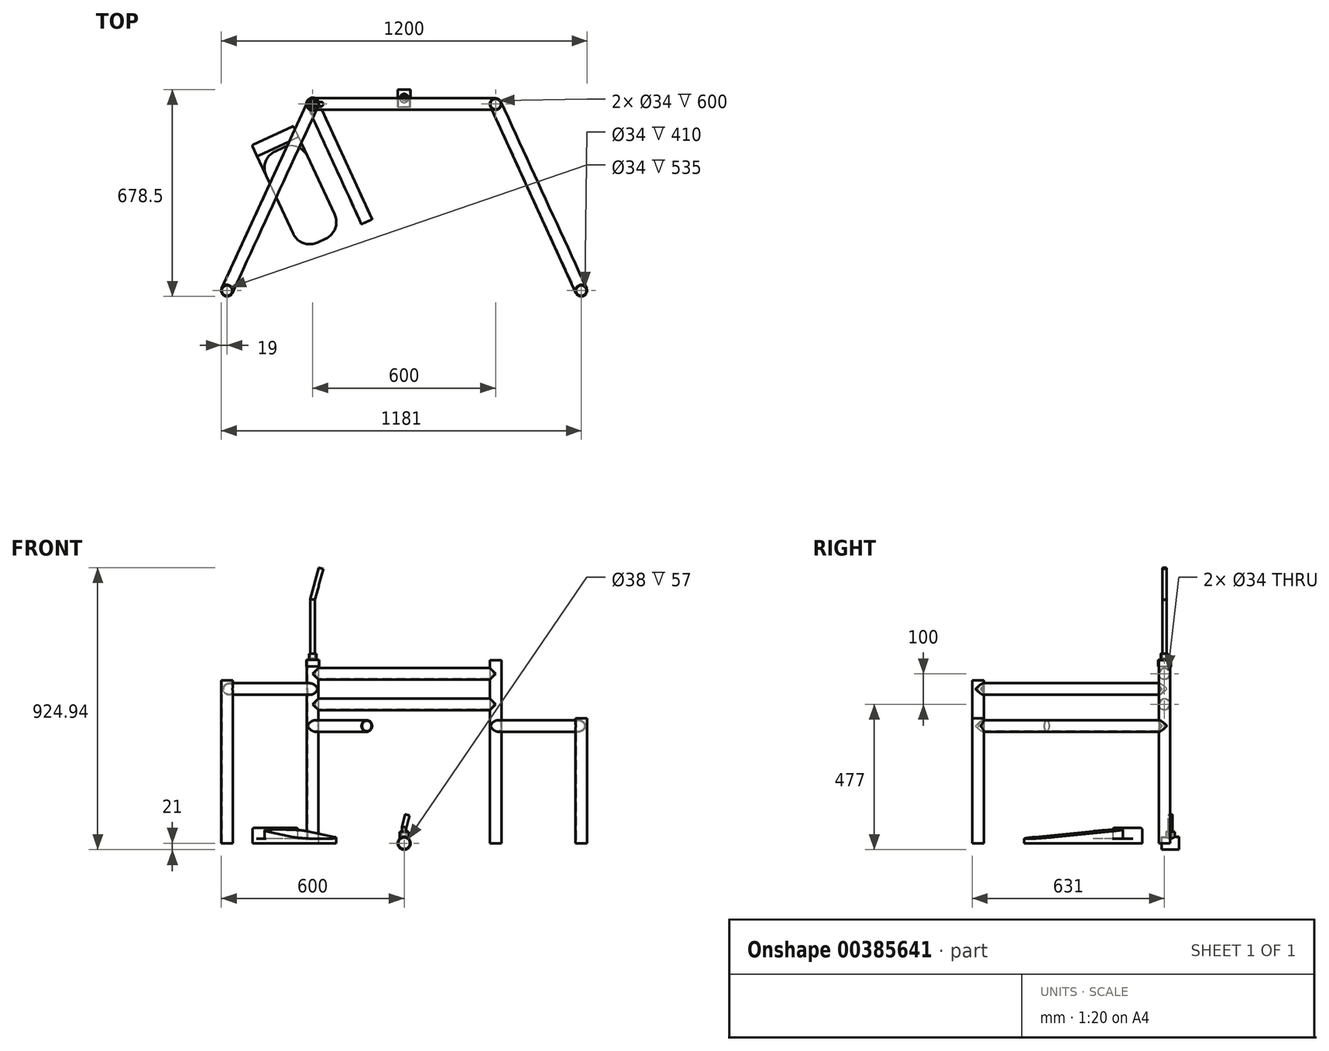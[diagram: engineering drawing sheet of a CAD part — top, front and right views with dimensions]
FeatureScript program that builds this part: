
annotation { "Feature Type Name" : "Feature", "Feature Type Description" : "" }
export const myFeature = defineFeature(function(context is Context, id is Id, definition is map)
    precondition{}
    {
        {
            assignVariable(context, id + "F0", {"name" : "tubo", "anyValue" : 38 * mm});
        }
        {
            var Q0;
            Q0=qCreatedBy(makeId("Top.planeOp"),FACE);
            var sketch = newSketch(context, id + "F1", { "sketchPlane" : qUnion([Q0])});
            skLineSegment(sketch, "E0.bottom", {"start": v(-600, 0) * mm, "end": v(600, 0) * mm});
            skLineSegment(sketch, "E0.top", {"start": v(-600, -650) * mm, "end": v(600, -650) * mm});
            skLineSegment(sketch, "E0.left", {"start": v(-600, 0) * mm, "end": v(-600, -650) * mm});
            skLineSegment(sketch, "E0.right", {"start": v(600, 0) * mm, "end": v(600, -650) * mm});
            skLineSegment(sketch, "E1.bottom", {"start": v(-650, 0) * mm, "end": v(650, 0) * mm});
            skLineSegment(sketch, "E1.top", {"start": v(-650, -1200) * mm, "end": v(650, -1200) * mm});
            skLineSegment(sketch, "E1.left", {"start": v(-650, 0) * mm, "end": v(-650, -1200) * mm});
            skLineSegment(sketch, "E1.right", {"start": v(650, 0) * mm, "end": v(650, -1200) * mm});
            skCircle(sketch, "E2", {"center": v(0, -1047.5) * mm, "radius": 152.5 * mm});
            skLineSegment(sketch, "E3.bottom", {"start": v(-581, -19) * mm, "end": v(581, -19) * mm, "construction": true});
            skLineSegment(sketch, "E3.top", {"start": v(-581, -631) * mm, "end": v(581, -631) * mm, "construction": true});
            skLineSegment(sketch, "E3.left", {"start": v(-581, -19) * mm, "end": v(-581, -631) * mm, "construction": true});
            skLineSegment(sketch, "E3.right", {"start": v(581, -19) * mm, "end": v(581, -631) * mm, "construction": true});
            skLineSegment(sketch, "E4.bottom", {"start": v(-300, -19) * mm, "end": v(300, -19) * mm, "construction": true});
            skLineSegment(sketch, "E4.top", {"start": v(-300, -631) * mm, "end": v(300, -631) * mm, "construction": true});
            skLineSegment(sketch, "E4.left", {"start": v(-300, -19) * mm, "end": v(-300, -631) * mm, "construction": true});
            skLineSegment(sketch, "E4.right", {"start": v(300, -19) * mm, "end": v(300, -631) * mm, "construction": true});
            skCircle(sketch, "E5", {"center": v(-581, -631) * mm, "radius": 19 * mm});
            skCircle(sketch, "E6", {"center": v(-581, -631) * mm, "radius": 17 * mm});
            skCircle(sketch, "E7", {"center": v(581, -631) * mm, "radius": 19 * mm});
            skCircle(sketch, "E8", {"center": v(581, -631) * mm, "radius": 17 * mm});
            skCircle(sketch, "E9", {"center": v(300, -19) * mm, "radius": 19 * mm});
            skCircle(sketch, "E10", {"center": v(300, -19) * mm, "radius": 17 * mm});
            skCircle(sketch, "E11", {"center": v(-300, -19) * mm, "radius": 19 * mm});
            skCircle(sketch, "E12", {"center": v(-300, -19) * mm, "radius": 17 * mm});
            skLineSegment(sketch, "E13", {"start": v(-300, -19) * mm, "end": v(-581, -631) * mm, "construction": true});
            skLineSegment(sketch, "E14", {"start": v(581, -631) * mm, "end": v(300, -19) * mm, "construction": true});
            skLineSegment(sketch, "E15", {"start": v(-476.85, -308.3) * mm, "end": v(-404.15, -341.7) * mm, "construction": true});
            skLineSegment(sketch, "E16", {"start": v(404.15, -341.7) * mm, "end": v(476.85, -308.3) * mm, "construction": true});
            skLineSegment(sketch, "E17", {"start": v(-300, -19) * mm, "end": v(-91.37, -473.4) * mm, "construction": true});
            skLineSegment(sketch, "E18", {"start": v(-136.8, -494.26) * mm, "end": v(-45.93, -452.53) * mm, "construction": true});
            skLineSegment(sketch, "E19", {"start": v(0, -1047.5) * mm, "end": v(-389.1, -213.06) * mm, "construction": true});
            skSolve(sketch);
        }
        {
            var Q0;
            Q0=makeQuery(id+"F1.imprint","IMPRINT",FACE,{"disambiguationData":[TD([[makeQuery(id+"F1.imprint","IMPRINT",EDGE,{"derivedFrom":sQuery(id+"F1.wireOp",EDGE,"E11")}),1.0]])]});
            var Q1;
            Q1=makeQuery(id+"F1.imprint","IMPRINT",FACE,{"disambiguationData":[TD([[makeQuery(id+"F1.imprint","IMPRINT",EDGE,{"derivedFrom":sQuery(id+"F1.wireOp",EDGE,"E9")}),1.0]])]});
            extrude(context, id + "F2", {"entities" : qUnion([Q0, Q1]), "depth" : 600 * mm});
        }
        {
            var Q0;
            Q0=makeQuery(id+"F1.imprint","IMPRINT",FACE,{"disambiguationData":[TD([[makeQuery(id+"F1.imprint","IMPRINT",EDGE,{"derivedFrom":sQuery(id+"F1.wireOp",EDGE,"E6")}),-1.0]])]});
            var Q1;
            Q1=makeQuery(id+"F1.imprint","IMPRINT",FACE,{"disambiguationData":[TD([[makeQuery(id+"F1.imprint","IMPRINT",EDGE,{"derivedFrom":sQuery(id+"F1.wireOp",EDGE,"E8")}),-1.0]])]});
            extrude(context, id + "F3", {"entities" : qUnion([Q0, Q1]), "depth" : 535 * mm});
        }
        {
            var Q0;
            Q0=qCreatedBy(makeId("Right.planeOp"),FACE);
            var sketch = newSketch(context, id + "F4", { "sketchPlane" : qUnion([Q0])});
            skCircle(sketch, "E20", {"center": v(-19, 556) * mm, "radius": 19 * mm});
            skCircle(sketch, "E21", {"center": v(-19, 556) * mm, "radius": 17 * mm});
            skLineSegment(sketch, "E22", {"start": v(-19, 556) * mm, "end": v(-19, 456) * mm, "construction": true});
            skCircle(sketch, "E23", {"center": v(-19, 456) * mm, "radius": 17 * mm});
            skCircle(sketch, "E24", {"center": v(-19, 456) * mm, "radius": 19 * mm});
            skLineSegment(sketch, "E25", {"start": v(-19, 556) * mm, "end": v(-19, 575) * mm, "construction": true});
            skPoint(sketch, "E26", {"position": v(-19, 506) * mm});
            skSolve(sketch);
        }
        {
            var Q0;
            Q0=makeQuery(id+"F4.imprint","IMPRINT",FACE,{"disambiguationData":[TD([[makeQuery(id+"F4.imprint","IMPRINT",EDGE,{"derivedFrom":sQuery(id+"F4.wireOp",EDGE,"E23")}),-1.0]])]});
            var Q1;
            Q1=makeQuery(id+"F4.imprint","IMPRINT",FACE,{"disambiguationData":[TD([[makeQuery(id+"F4.imprint","IMPRINT",EDGE,{"derivedFrom":sQuery(id+"F4.wireOp",EDGE,"E20")}),1.0]])]});
            var Q2;
            Q2=makeQuery(id+"F2.opExtrude","SWEPT_FACE",FACE,{"disambiguationData":[OSD([sQuery(id+"F1.wireOp",EDGE,"E9")])]});
            var Q3;
            Q3=makeQuery(id+"F2.opExtrude","SWEPT_FACE",FACE,{"disambiguationData":[OSD([sQuery(id+"F1.wireOp",EDGE,"E11")])]});
            extrude(context, id + "F5", {"entities" : qUnion([Q0, Q1]), "operationType" : NewBodyOperationType.ADD, "endBound" : BoundingType.UP_TO_SURFACE, "endBoundEntityFace" : qUnion([Q2]), "depth" : 25 * mm, "hasSecondDirection" : true, "secondDirectionBound" : SecondDirectionBoundingType.UP_TO_SURFACE, "secondDirectionOppositeDirection" : true, "secondDirectionBoundEntityFace" : qUnion([Q3]), "secondDirectionDepth" : 25 * mm});
        }
        {
            var Q0;
            Q0=sQuery(id+"F1.wireOp",EDGE,"E15");
            cPlane(context, id + "F6", {"entities" : qUnion([Q0]), "cplaneType" : CPlaneType.LINE_ANGLE, "offset" : 25 * mm, "angle" : 0 * degree, "width" : 150 * mm, "height" : 150 * mm});
        }
        {
            var Q0;
            Q0=qCreatedBy(id+"F6.planeOp",FACE);
            var sketch = newSketch(context, id + "F7", { "sketchPlane" : qUnion([Q0])});
            skCircle(sketch, "E27", {"center": v(264.7, 506) * mm, "radius": 19 * mm});
            skCircle(sketch, "E28", {"center": v(264.7, 506) * mm, "radius": 17 * mm});
            skLineSegment(sketch, "E29", {"start": v(264.7, 506) * mm, "end": v(264.7, 0) * mm, "construction": true});
            skLineSegment(sketch, "E30", {"start": v(264.7, 506) * mm, "end": v(264.7, 525) * mm, "construction": true});
            skSolve(sketch);
        }
        {
            var Q0;
            Q0=makeQuery(id+"F7.imprint","IMPRINT",FACE,{"disambiguationData":[TD([[makeQuery(id+"F7.imprint","IMPRINT",EDGE,{"derivedFrom":sQuery(id+"F7.wireOp",EDGE,"E27")}),1.0]])]});
            var Q1;
            {var subQ1=sQuery(id+"F1.wireOp",EDGE,"E11");Q1=makeQuery(id+"F5.boolean.opBoolean","SPLIT",FACE,{"disambiguationData":[TD([makeQuery(id+"F5.opExtrude","SWEPT_FACE",FACE,{"disambiguationData":[OSD([sQuery(id+"F4.wireOp",EDGE,"E20")])]})])],"derivedFrom":makeQuery(id+"F2.opExtrude","SWEPT_FACE",FACE,{"disambiguationData":[OSD([subQ1])]})});}
            var Q2;
            Q2=makeQuery(id+"F3.opExtrude","SWEPT_FACE",FACE,{"disambiguationData":[OSD([sQuery(id+"F1.wireOp",EDGE,"E5")])]});
            extrude(context, id + "F8", {"entities" : qUnion([Q0]), "operationType" : NewBodyOperationType.ADD, "endBound" : BoundingType.UP_TO_SURFACE, "endBoundEntityFace" : qUnion([Q1]), "depth" : 25 * mm, "hasSecondDirection" : true, "secondDirectionBound" : SecondDirectionBoundingType.UP_TO_SURFACE, "secondDirectionOppositeDirection" : true, "secondDirectionBoundEntityFace" : qUnion([Q2]), "secondDirectionDepth" : 25 * mm});
        }
        {
            var Q0;
            Q0=sQuery(id+"F1.wireOp",EDGE,"E16");
            cPlane(context, id + "F9", {"entities" : qUnion([Q0]), "cplaneType" : CPlaneType.LINE_ANGLE, "offset" : 25 * mm, "angle" : 0 * degree, "width" : 150 * mm, "height" : 150 * mm});
        }
        {
            var Q0;
            Q0=qCreatedBy(id+"F9.planeOp",FACE);
            var sketch = newSketch(context, id + "F10", { "sketchPlane" : qUnion([Q0])});
            skCircle(sketch, "E31", {"center": v(-264.7, 385) * mm, "radius": 19 * mm});
            skCircle(sketch, "E32", {"center": v(-264.7, 385) * mm, "radius": 17 * mm});
            skLineSegment(sketch, "E33", {"start": v(-264.7, 385) * mm, "end": v(-264.7, 0) * mm, "construction": true});
            skLineSegment(sketch, "E34", {"start": v(-264.7, 385) * mm, "end": v(-264.7, 404) * mm, "construction": true});
            skSolve(sketch);
        }
        {
            var Q0;
            Q0=makeQuery(id+"F10.imprint","IMPRINT",FACE,{"disambiguationData":[TD([[makeQuery(id+"F10.imprint","IMPRINT",EDGE,{"derivedFrom":sQuery(id+"F10.wireOp",EDGE,"E31")}),1.0]])]});
            var Q1;
            {var subQ1=sQuery(id+"F1.wireOp",EDGE,"E9");Q1=makeQuery(id+"F5.boolean.opBoolean","SPLIT",FACE,{"disambiguationData":[TD([makeQuery(id+"F5.opExtrude","SWEPT_FACE",FACE,{"disambiguationData":[OSD([sQuery(id+"F4.wireOp",EDGE,"E20")])]})])],"derivedFrom":makeQuery(id+"F2.opExtrude","SWEPT_FACE",FACE,{"disambiguationData":[OSD([subQ1])]})});}
            var Q2;
            Q2=makeQuery(id+"F3.opExtrude","SWEPT_FACE",FACE,{"disambiguationData":[OSD([sQuery(id+"F1.wireOp",EDGE,"E7")])]});
            extrude(context, id + "F11", {"entities" : qUnion([Q0]), "operationType" : NewBodyOperationType.ADD, "endBound" : BoundingType.UP_TO_SURFACE, "endBoundEntityFace" : qUnion([Q1]), "depth" : 25 * mm, "hasSecondDirection" : true, "secondDirectionBound" : SecondDirectionBoundingType.UP_TO_SURFACE, "secondDirectionOppositeDirection" : true, "secondDirectionBoundEntityFace" : qUnion([Q2]), "secondDirectionDepth" : 25 * mm});
        }
        {
            var Q0;
            Q0=sQuery(id+"F1.wireOp",EDGE,"E18");
            cPlane(context, id + "F12", {"entities" : qUnion([Q0]), "cplaneType" : CPlaneType.LINE_ANGLE, "offset" : 25 * mm, "angle" : 0 * degree, "width" : 150 * mm, "height" : 150 * mm});
        }
        {
            var Q0;
            Q0=qCreatedBy(id+"F12.planeOp",FACE);
            var sketch = newSketch(context, id + "F13", { "sketchPlane" : qUnion([Q0])});
            skCircle(sketch, "E35", {"center": v(280.56, 385) * mm, "radius": 19 * mm});
            skCircle(sketch, "E36", {"center": v(280.56, 385) * mm, "radius": 17 * mm});
            skLineSegment(sketch, "E37", {"start": v(280.56, 385) * mm, "end": v(280.56, 0) * mm, "construction": true});
            skSolve(sketch);
        }
        {
            var Q0;
            Q0=makeQuery(id+"F13.imprint","IMPRINT",FACE,{"disambiguationData":[TD([[makeQuery(id+"F13.imprint","IMPRINT",EDGE,{"derivedFrom":sQuery(id+"F13.wireOp",EDGE,"E35")}),1.0]])]});
            var Q1;
            {var subQ1=makeQuery(id+"F5.opExtrude","SWEPT_FACE",FACE,{"disambiguationData":[OSD([sQuery(id+"F4.wireOp",EDGE,"E20")])]});var subQ3=sQuery(id+"F1.wireOp",EDGE,"E11");Q1=makeQuery(id+"F8.boolean.opBoolean","SPLIT",FACE,{"disambiguationData":[TD([subQ1])],"derivedFrom":makeQuery(id+"F5.boolean.opBoolean","SPLIT",FACE,{"disambiguationData":[TD([subQ1])],"derivedFrom":makeQuery(id+"F2.opExtrude","SWEPT_FACE",FACE,{"disambiguationData":[OSD([subQ3])]})})});}
            extrude(context, id + "F14", {"entities" : qUnion([Q0]), "operationType" : NewBodyOperationType.ADD, "endBound" : BoundingType.UP_TO_SURFACE, "endBoundEntityFace" : qUnion([Q1]), "depth" : 25 * mm, "hasSecondDirection" : true, "secondDirectionOppositeDirection" : false, "secondDirectionDepth" : 75 * mm});
        }
        {
            var Q0;
            Q0=qCreatedBy(makeId("Front.planeOp"),FACE);
            var sketch = newSketch(context, id + "F15", { "sketchPlane" : qUnion([Q0])});
            skCircle(sketch, "E38", {"center": v(0, 0) * mm, "radius": 21 * mm});
            skCircle(sketch, "E39", {"center": v(0, 0) * mm, "radius": 19 * mm});
            skSolve(sketch);
        }
        {
            var Q0;
            Q0 = qSketchRegion(id + "F15", true);
            extrude(context, id + "F16", {"entities" : qUnion([Q0]), "depth" : getVariable(context, 'tubo') * 0.75, "hasSecondDirection" : true, "secondDirectionOppositeDirection" : true, "secondDirectionDepth" : getVariable(context, 'tubo') * 0.75});
        }
        {
            var Q0;
            Q0=qCreatedBy(makeId("Top.planeOp"),FACE);
            var sketch = newSketch(context, id + "F17", { "sketchPlane" : qUnion([Q0])});
            skCircle(sketch, "E40", {"center": v(0, 0) * mm, "radius": 14.25 * mm});
            skSolve(sketch);
        }
        {
            var Q0;
            Q0=makeQuery(id+"F17.imprint","IMPRINT",FACE,{"disambiguationData":[TD([[makeQuery(id+"F17.imprint","IMPRINT",EDGE,{"derivedFrom":sQuery(id+"F17.wireOp",EDGE,"E40")}),1.0]])]});
            var Q1;
            Q1=sQuery(id+"F17.wireOp",EDGE,"E40");
            var Q2;
            Q2=makeQuery(id+"F16.opExtrude","SWEPT_FACE",FACE,{"disambiguationData":[OSD([sQuery(id+"F15.wireOp",EDGE,"E38")])]});
            extrude(context, id + "F18", {"entities" : qUnion([Q0]), "operationType" : NewBodyOperationType.ADD, "surfaceEntities" : qUnion([Q1]), "depth" : getVariable(context, 'tubo'), "hasSecondDirection" : true, "secondDirectionBound" : SecondDirectionBoundingType.UP_TO_SURFACE, "secondDirectionOppositeDirection" : false, "secondDirectionBoundEntityFace" : qUnion([Q2]), "secondDirectionDepth" : 25 * mm});
        }
        {
            var Q0;
            Q0=makeQuery(id+"F18.opExtrude","CAP_FACE",FACE,{"disambiguationData":[OSD([sQuery(id+"F17.wireOp",EDGE,"E40")])],"isStart":false});
            var sketch = newSketch(context, id + "F19", { "sketchPlane" : qUnion([Q0])});
            skCircle(sketch, "E41", {"center": v(0, 0) * mm, "radius": 7.5 * mm});
            skSolve(sketch);
        }
        {
            var Q0;
            Q0=makeQuery(id+"F19.imprint","IMPRINT",FACE,{"disambiguationData":[TD([[makeQuery(id+"F19.imprint","IMPRINT",EDGE,{"derivedFrom":sQuery(id+"F19.wireOp",EDGE,"E41")}),1.0]])]});
            extrude(context, id + "F20", {"entities" : qUnion([Q0]), "operationType" : NewBodyOperationType.REMOVE, "oppositeDirection" : true, "depth" : 15 * mm});
        }
        {
            var Q0;
            Q0=qCreatedBy(makeId("Front.planeOp"),FACE);
            var sketch = newSketch(context, id + "F21", { "sketchPlane" : qUnion([Q0])});
            skLineSegment(sketch, "E42", {"start": v(0, 23) * mm, "end": v(0, 53) * mm});
            skLineSegment(sketch, "E43", {"start": v(0, 53) * mm, "end": v(10.72, 93) * mm});
            skSolve(sketch);
        }
        {
            var Q0;
            Q0=makeQuery(id+"F20.boolean.opBoolean","COPY",FACE,{"derivedFrom":makeQuery(id+"F20.opExtrude","CAP_FACE",FACE,{"disambiguationData":[OSD([sQuery(id+"F19.wireOp",EDGE,"E41")])],"isStart":false})});
            var Q1;
            Q1=sQuery(id+"F21.wireOp",EDGE,"E42");
            var Q2;
            Q2=sQuery(id+"F21.wireOp",EDGE,"E43");
            sweep(context, id + "F22", {"profiles" : qUnion([Q0]), "path" : qUnion([Q1, Q2])});
        }
        {
            var Q0;
            Q0=makeQuery(id+"F3.opExtrude","CAP_FACE",FACE,{"disambiguationData":[OSD([sQuery(id+"F1.wireOp",EDGE,"E7"),sQuery(id+"F1.wireOp",EDGE,"E8")])],"isStart":false});
            var sketch = newSketch(context, id + "F23", { "sketchPlane" : qUnion([Q0])});
            skCircle(sketch, "E44", {"center": v(581, -631) * mm, "radius": 19 * mm});
            skSolve(sketch);
        }
        {
            var Q0;
            Q0 = qSketchRegion(id + "F23", true);
            extrude(context, id + "F24", {"entities" : qUnion([Q0]), "operationType" : NewBodyOperationType.REMOVE, "oppositeDirection" : true, "depth" : 125 * mm});
        }
        {
            var Q0;
            Q0=makeQuery(id+"F2.opExtrude","CAP_FACE",FACE,{"disambiguationData":[OSD([sQuery(id+"F1.wireOp",EDGE,"E11"),sQuery(id+"F1.wireOp",EDGE,"E12")])],"isStart":false});
            var sketch = newSketch(context, id + "F25", { "sketchPlane" : qUnion([Q0])});
            skCircle(sketch, "E45", {"center": v(-300, -19) * mm, "radius": 21 * mm});
            skCircle(sketch, "E46", {"center": v(-300, -19) * mm, "radius": 19 * mm});
            skCircle(sketch, "E47", {"center": v(-300, -19) * mm, "radius": 7.5 * mm});
            skCircle(sketch, "E48", {"center": v(-300, -19) * mm, "radius": 12.5 * mm});
            skSolve(sketch);
        }
        {
            var Q0;
            Q0=makeQuery(id+"F25.imprint","IMPRINT",FACE,{"disambiguationData":[TD([[makeQuery(id+"F25.imprint","IMPRINT",EDGE,{"derivedFrom":sQuery(id+"F25.wireOp",EDGE,"E45")}),1.0]])]});
            extrude(context, id + "F26", {"entities" : qUnion([Q0]), "oppositeDirection" : true, "depth" : 20 * mm});
        }
        {
            var Q0;
            Q0=makeQuery(id+"F25.imprint","IMPRINT",FACE,{"disambiguationData":[TD([[makeQuery(id+"F25.imprint","IMPRINT",EDGE,{"derivedFrom":sQuery(id+"F25.wireOp",EDGE,"E45")}),1.0]])]});
            var Q1;
            Q1=makeQuery(id+"F25.imprint","IMPRINT",FACE,{"disambiguationData":[TD([[makeQuery(id+"F25.imprint","IMPRINT",EDGE,{"derivedFrom":sQuery(id+"F25.wireOp",EDGE,"E46")}),1.0]])]});
            var Q2;
            Q2=makeQuery(id+"F25.imprint","IMPRINT",FACE,{"disambiguationData":[TD([[makeQuery(id+"F25.imprint","IMPRINT",EDGE,{"derivedFrom":sQuery(id+"F25.wireOp",EDGE,"E48")}),-1.0]])]});
            var Q3;
            Q3=makeQuery(id+"F25.imprint","IMPRINT",FACE,{"disambiguationData":[TD([[makeQuery(id+"F25.imprint","IMPRINT",EDGE,{"derivedFrom":sQuery(id+"F25.wireOp",EDGE,"E47")}),-1.0]])]});
            var Q4;
            Q4=makeQuery(id+"F25.imprint","IMPRINT",FACE,{"disambiguationData":[TD([[makeQuery(id+"F25.imprint","IMPRINT",EDGE,{"derivedFrom":sQuery(id+"F25.wireOp",EDGE,"E47")}),1.0]])]});
            extrude(context, id + "F27", {"entities" : qUnion([Q0, Q1, Q2, Q3, Q4]), "operationType" : NewBodyOperationType.ADD, "depth" : 2 * mm});
        }
        {
            var Q0;
            Q0=makeQuery(id+"F25.imprint","IMPRINT",FACE,{"disambiguationData":[TD([[makeQuery(id+"F25.imprint","IMPRINT",EDGE,{"derivedFrom":sQuery(id+"F25.wireOp",EDGE,"E47")}),-1.0]])]});
            var Q1;
            Q1=makeQuery(id+"F25.imprint","IMPRINT",FACE,{"disambiguationData":[TD([[makeQuery(id+"F25.imprint","IMPRINT",EDGE,{"derivedFrom":sQuery(id+"F25.wireOp",EDGE,"E47")}),1.0]])]});
            extrude(context, id + "F28", {"entities" : qUnion([Q0, Q1]), "operationType" : NewBodyOperationType.ADD, "depth" : 7 * mm});
        }
        {
            var Q0;
            Q0=makeQuery(id+"F25.imprint","IMPRINT",FACE,{"disambiguationData":[TD([[makeQuery(id+"F25.imprint","IMPRINT",EDGE,{"derivedFrom":sQuery(id+"F25.wireOp",EDGE,"E47")}),-1.0]])]});
            extrude(context, id + "F29", {"entities" : qUnion([Q0]), "operationType" : NewBodyOperationType.ADD, "depth" : 22 * mm});
        }
        {
            var Q0;
            Q0=qCreatedBy(makeId("Front.planeOp"),FACE);
            var sketch = newSketch(context, id + "F30", { "sketchPlane" : qUnion([Q0])});
            skLineSegment(sketch, "E49", {"start": v(-300, 600) * mm, "end": v(-300, 800) * mm});
            skLineSegment(sketch, "E50", {"start": v(-300, 800) * mm, "end": v(-272.67, 902) * mm});
            skSolve(sketch);
        }
        {
            var Q0;
            Q0=makeQuery(id+"F28.opExtrude","CAP_FACE",FACE,{"disambiguationData":[OSD([sQuery(id+"F25.wireOp",EDGE,"E48")])],"isStart":false});
            var Q1;
            Q1=sQuery(id+"F30.wireOp",EDGE,"E49");
            var Q2;
            Q2=sQuery(id+"F30.wireOp",EDGE,"E50");
            sweep(context, id + "F31", {"profiles" : qUnion([Q0]), "path" : qUnion([Q1, Q2])});
        }
        {
            var Q0;
            Q0=qCreatedBy(makeId("Top.planeOp"),FACE);
            var sketch = newSketch(context, id + "F32", { "sketchPlane" : qUnion([Q0])});
            skLineSegment(sketch, "E51.bottom", {"start": v(-499.34, -154.13) * mm, "end": v(-363.4, -90.74) * mm});
            skLineSegment(sketch, "E51.top", {"start": v(-338.74, -498.53) * mm, "end": v(-202.8, -435.13) * mm});
            skLineSegment(sketch, "E51.left", {"start": v(-499.34, -154.13) * mm, "end": v(-338.74, -498.53) * mm});
            skLineSegment(sketch, "E51.right", {"start": v(-363.4, -90.74) * mm, "end": v(-202.8, -435.13) * mm});
            skLineSegment(sketch, "E52", {"start": v(-482.43, -190.38) * mm, "end": v(-346.49, -126.99) * mm});
            skLineSegment(sketch, "E53", {"start": v(-478.2, -199.44) * mm, "end": v(-342.26, -136.05) * mm});
            skSolve(sketch);
        }
        {
            var Q0;
            {var subQ0=sQuery(id+"F32.wireOp",EDGE,"E51.top");Q0=makeQuery(id+"F32.imprint","IMPRINT",FACE,{"disambiguationData":[TD([[makeQuery(id+"F32.imprint","IMPRINT",EDGE,{"derivedFrom":subQ0}),1.0]])]});}
            var Q1;
            {var subQ0=sQuery(id+"F32.wireOp",EDGE,"E52");Q1=makeQuery(id+"F32.imprint","IMPRINT",FACE,{"disambiguationData":[TD([[makeQuery(id+"F32.imprint","IMPRINT",EDGE,{"derivedFrom":subQ0}),-1.0]])]});}
            var Q2;
            {var subQ0=sQuery(id+"F32.wireOp",EDGE,"E51.bottom");Q2=makeQuery(id+"F32.imprint","IMPRINT",FACE,{"disambiguationData":[TD([[makeQuery(id+"F32.imprint","IMPRINT",EDGE,{"derivedFrom":subQ0}),-1.0]])]});}
            extrude(context, id + "F33", {"entities" : qUnion([Q0, Q1, Q2]), "depth" : 15 * mm});
        }
        {
            var Q0;
            {var subQ0=sQuery(id+"F32.wireOp",EDGE,"E51.bottom");Q0=makeQuery(id+"F32.imprint","IMPRINT",FACE,{"disambiguationData":[TD([[makeQuery(id+"F32.imprint","IMPRINT",EDGE,{"derivedFrom":subQ0}),-1.0]])]});}
            extrude(context, id + "F34", {"entities" : qUnion([Q0]), "operationType" : NewBodyOperationType.ADD, "depth" : 50 * mm});
        }
        {
            var Q0;
            {var subQ0=sQuery(id+"F32.wireOp",EDGE,"E51.top");Q0=makeQuery(id+"F32.imprint","IMPRINT",FACE,{"disambiguationData":[TD([[makeQuery(id+"F32.imprint","IMPRINT",EDGE,{"derivedFrom":subQ0}),1.0]])]});}
            extrude(context, id + "F35", {"entities" : qUnion([Q0]), "operationType" : NewBodyOperationType.ADD, "depth" : 45 * mm});
        }
        {
            var Q0;
            Q0=makeQuery(id+"F35.opExtrude","CAP_EDGE",EDGE,{"disambiguationData":[OSD([sQuery(id+"F32.wireOp",EDGE,"E51.top")])],"isStart":false});
            chamfer(context, id + "F36", {"entities" : qUnion([Q0]), "chamferType" : ChamferType.TWO_OFFSETS, "width1" : 330 * mm, "oppositeDirection" : false, "width2" : 30 * mm, "tangentPropagation" : true});
        }
        {
            var Q0;
            {var subQ0=sQuery(id+"F32.wireOp",EDGE,"E51.right");var subQ1=sQuery(id+"F32.wireOp",EDGE,"E51.top");Q0=makeQuery(id+"F35.boolean.opBoolean","MERGE",EDGE,{"derivedFrom":[makeQuery(id+"F33.opExtrude","SWEPT_EDGE",EDGE,{"disambiguationData":[OSD([subQ1,subQ0])]}),makeQuery(id+"F35.opExtrude","SWEPT_EDGE",EDGE,{"disambiguationData":[OSD([subQ1,subQ0])]})]});}
            var Q1;
            {var subQ0=sQuery(id+"F32.wireOp",EDGE,"E51.left");var subQ1=sQuery(id+"F32.wireOp",EDGE,"E51.top");Q1=makeQuery(id+"F35.boolean.opBoolean","MERGE",EDGE,{"derivedFrom":[makeQuery(id+"F33.opExtrude","SWEPT_EDGE",EDGE,{"disambiguationData":[OSD([subQ1,subQ0])]}),makeQuery(id+"F35.opExtrude","SWEPT_EDGE",EDGE,{"disambiguationData":[OSD([subQ1,subQ0])]})]});}
            var Q2;
            Q2=makeQuery(id+"F35.opExtrude","SWEPT_EDGE",EDGE,{"disambiguationData":[OSD([sQuery(id+"F32.wireOp",EDGE,"E51.right"),sQuery(id+"F32.wireOp",EDGE,"E53")])]});
            var Q3;
            Q3=makeQuery(id+"F35.opExtrude","SWEPT_EDGE",EDGE,{"disambiguationData":[OSD([sQuery(id+"F32.wireOp",EDGE,"E51.left"),sQuery(id+"F32.wireOp",EDGE,"E53")])]});
            fillet(context, id + "F37", {"entities" : qUnion([Q0, Q1, Q2, Q3]), "radius" : 60 * mm, "tangentPropagation" : true, "allowEdgeOverflow" : false});
        }
        {
            var Q0;
            Q0=makeQuery(id+"F34.opExtrude","SWEPT_EDGE",EDGE,{"disambiguationData":[OSD([sQuery(id+"F32.wireOp",EDGE,"E51.left"),sQuery(id+"F32.wireOp",EDGE,"E52")])]});
            var Q1;
            {var subQ0=sQuery(id+"F32.wireOp",EDGE,"E51.left");var subQ1=sQuery(id+"F32.wireOp",EDGE,"E51.bottom");Q1=makeQuery(id+"F34.boolean.opBoolean","MERGE",EDGE,{"derivedFrom":[makeQuery(id+"F33.opExtrude","SWEPT_EDGE",EDGE,{"disambiguationData":[OSD([subQ1,subQ0])]}),makeQuery(id+"F34.opExtrude","SWEPT_EDGE",EDGE,{"disambiguationData":[OSD([subQ1,subQ0])]})]});}
            var Q2;
            Q2=makeQuery(id+"F34.opExtrude","SWEPT_EDGE",EDGE,{"disambiguationData":[OSD([sQuery(id+"F32.wireOp",EDGE,"E51.right"),sQuery(id+"F32.wireOp",EDGE,"E52")])]});
            var Q3;
            {var subQ0=sQuery(id+"F32.wireOp",EDGE,"E51.right");var subQ1=sQuery(id+"F32.wireOp",EDGE,"E51.bottom");Q3=makeQuery(id+"F34.boolean.opBoolean","MERGE",EDGE,{"derivedFrom":[makeQuery(id+"F33.opExtrude","SWEPT_EDGE",EDGE,{"disambiguationData":[OSD([subQ1,subQ0])]}),makeQuery(id+"F34.opExtrude","SWEPT_EDGE",EDGE,{"disambiguationData":[OSD([subQ1,subQ0])]})]});}
            var Q4;
            Q4=makeQuery(id+"F34.opExtrude","CAP_EDGE",EDGE,{"disambiguationData":[OSD([sQuery(id+"F32.wireOp",EDGE,"E52")])],"isStart":false});
            var Q5;
            Q5=makeQuery(id+"F34.opExtrude","CAP_EDGE",EDGE,{"disambiguationData":[OSD([sQuery(id+"F32.wireOp",EDGE,"E51.right")])],"isStart":false});
            var Q6;
            Q6=makeQuery(id+"F34.opExtrude","CAP_EDGE",EDGE,{"disambiguationData":[OSD([sQuery(id+"F32.wireOp",EDGE,"E51.bottom")])],"isStart":false});
            var Q7;
            Q7=makeQuery(id+"F34.opExtrude","CAP_EDGE",EDGE,{"disambiguationData":[OSD([sQuery(id+"F32.wireOp",EDGE,"E51.left")])],"isStart":false});
            fillet(context, id + "F38", {"entities" : qUnion([Q0, Q1, Q2, Q3, Q4, Q5, Q6, Q7]), "radius" : 5 * mm, "tangentPropagation" : true, "allowEdgeOverflow" : false});
        }
    });
